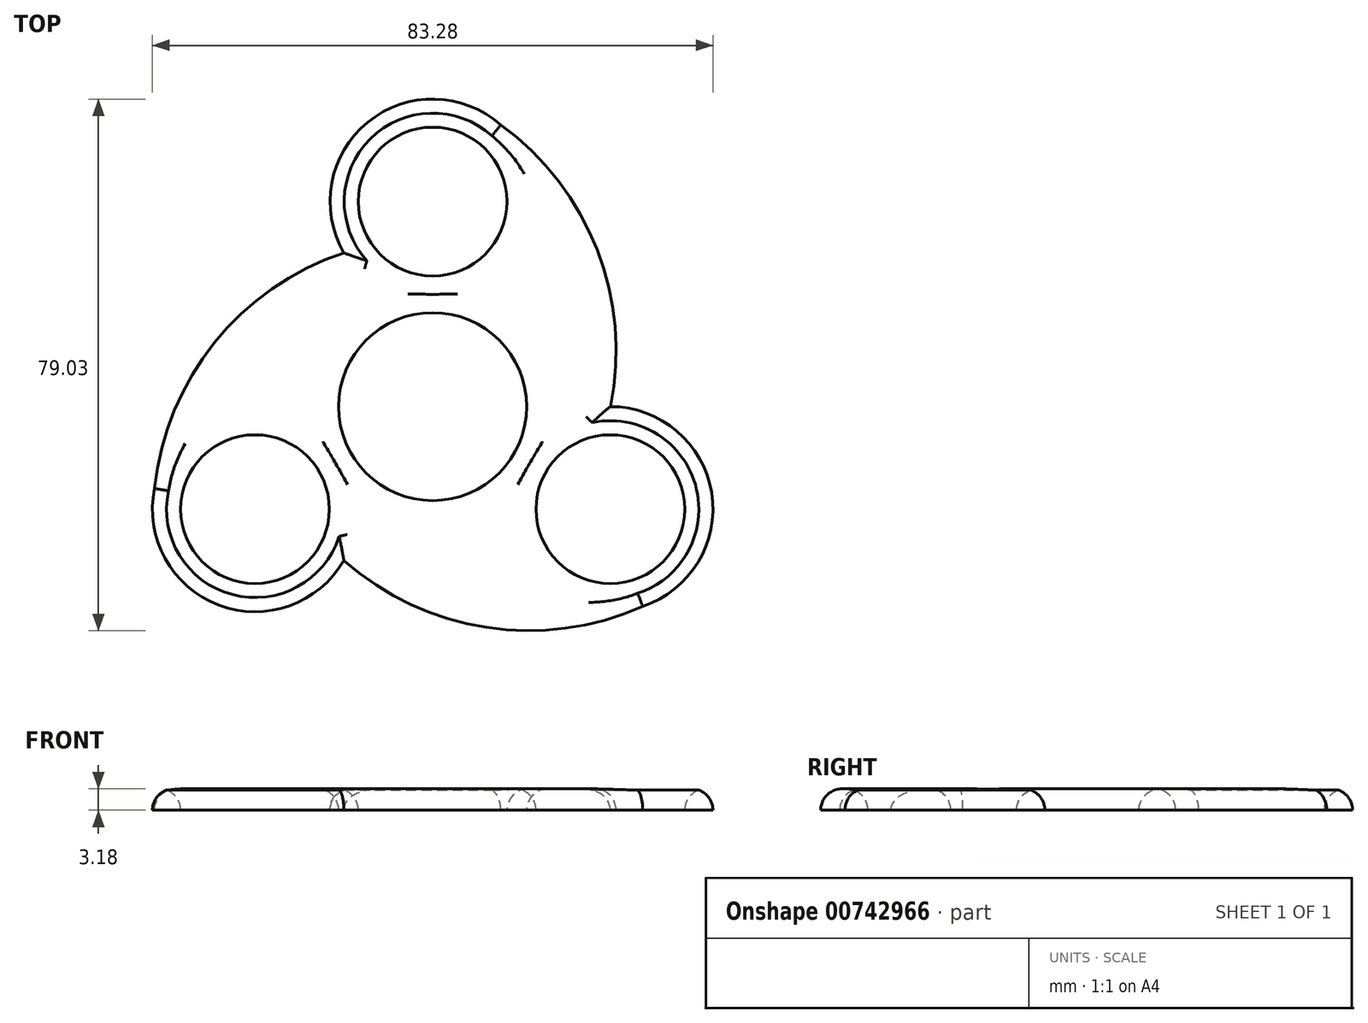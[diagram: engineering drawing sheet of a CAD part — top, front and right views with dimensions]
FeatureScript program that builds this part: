
annotation { "Feature Type Name" : "Feature", "Feature Type Description" : "" }
export const myFeature = defineFeature(function(context is Context, id is Id, definition is map)
    precondition{}
    {
        {
            var Q0;
            Q0=qCreatedBy(makeId("Top.planeOp"),FACE);
            var sketch = newSketch(context, id + "F0", { "sketchPlane" : qUnion([Q0])});
            skCircle(sketch, "E0", {"center": v(0, 0) * mm, "radius": 13.97 * mm});
            skCircle(sketch, "E1", {"center": v(0, 0) * mm, "radius": 11.05 * mm});
            skLineSegment(sketch, "E2", {"start": v(0, 0) * mm, "end": v(0, 30.48) * mm});
            skCircle(sketch, "E3", {"center": v(0, 30.48) * mm, "radius": 15.24 * mm});
            skCircle(sketch, "E4", {"center": v(0, 30.48) * mm, "radius": 11.05 * mm});
            skCircle(sketch, "E5.1.0", {"center": v(-26.4, -15.24) * mm, "radius": 15.24 * mm});
            skCircle(sketch, "E5.1.1", {"center": v(-26.4, -15.24) * mm, "radius": 11.05 * mm});
            skCircle(sketch, "E5.2.0", {"center": v(26.4, -15.24) * mm, "radius": 15.24 * mm});
            skCircle(sketch, "E5.2.1", {"center": v(26.4, -15.24) * mm, "radius": 11.05 * mm});
            skArc(sketch, "E6", {"start": v(26.4, 0) * mm, "mid": v(23.5, 25.53) * mm, "end": v(6.12, 44.44) * mm});
            skArc(sketch, "E7.1.1", {"start": v(-13.2, 22.86) * mm, "mid": v(-33.86, 7.6) * mm, "end": v(-41.54, -16.92) * mm});
            skArc(sketch, "E7.2.1", {"start": v(-13.2, -22.86) * mm, "mid": v(10.35, -33.12) * mm, "end": v(35.42, -27.52) * mm});
            skSolve(sketch);
        }
        {
            var Q0;
            Q0 = qSketchRegion(id + "F0", true);
            extrude(context, id + "F1", {"entities" : qUnion([Q0]), "depth" : 3.17 * mm, "offsetDistance" : 25.4 * mm});
        }
        {
            var Q0;
            Q0=makeQuery(id+"F1.opExtrude","CAP_FACE",FACE,{"disambiguationData":[OSD([sQuery(id+"F0.wireOp",EDGE,"E0"),sQuery(id+"F0.wireOp",EDGE,"E3"),sQuery(id+"F0.wireOp",EDGE,"E4"),sQuery(id+"F0.wireOp",EDGE,"E5.1.0"),sQuery(id+"F0.wireOp",EDGE,"E5.1.1"),sQuery(id+"F0.wireOp",EDGE,"E5.2.0"),sQuery(id+"F0.wireOp",EDGE,"E5.2.1"),sQuery(id+"F0.wireOp",EDGE,"E6"),sQuery(id+"F0.wireOp",EDGE,"E7.1.1"),sQuery(id+"F0.wireOp",EDGE,"E7.2.1")])],"isStart":false});
            var Q1;
            Q1=makeQuery(id+"F1.opExtrude","CAP_EDGE",EDGE,{"disambiguationData":[OSD([sQuery(id+"F0.wireOp",EDGE,"E6")])],"isStart":false});
            var Q2;
            Q2=makeQuery(id+"F1.opExtrude","CAP_EDGE",EDGE,{"disambiguationData":[OSD([sQuery(id+"F0.wireOp",EDGE,"E7.1.1")])],"isStart":false});
            var Q3;
            Q3=makeQuery(id+"F1.opExtrude","CAP_EDGE",EDGE,{"disambiguationData":[OSD([sQuery(id+"F0.wireOp",EDGE,"E7.2.1")])],"isStart":false});
            var Q4;
            Q4=makeQuery(id+"F1.opExtrude","CAP_EDGE",EDGE,{"disambiguationData":[OSD([sQuery(id+"F0.wireOp",EDGE,"E5.1.0")])],"isStart":false});
            var Q5;
            Q5=makeQuery(id+"F1.opExtrude","CAP_EDGE",EDGE,{"disambiguationData":[OSD([sQuery(id+"F0.wireOp",EDGE,"E3")])],"isStart":false});
            fillet(context, id + "F2", {"entities" : qUnion([Q0, Q1, Q2, Q3, Q4, Q5]), "radius" : 3.17 * mm, "tangentPropagation" : true, "allowEdgeOverflow" : false});
        }
    });
